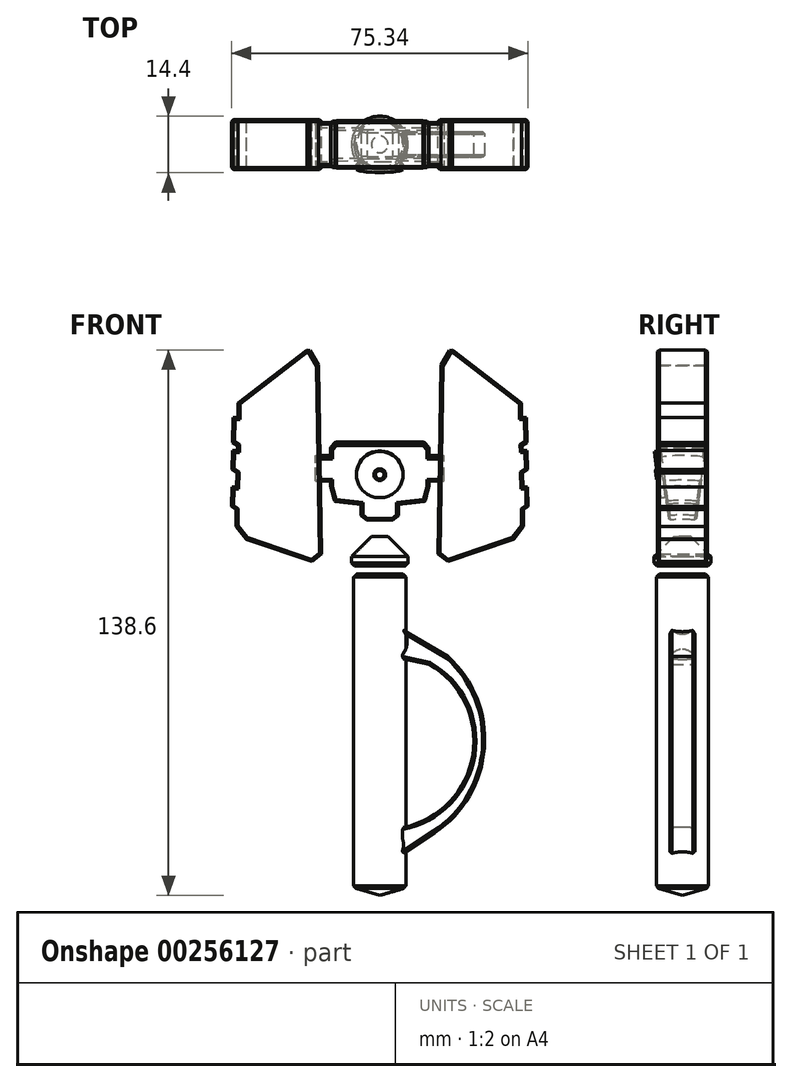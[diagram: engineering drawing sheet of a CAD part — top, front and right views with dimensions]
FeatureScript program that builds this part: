
annotation { "Feature Type Name" : "Feature", "Feature Type Description" : "" }
export const myFeature = defineFeature(function(context is Context, id is Id, definition is map)
    precondition{}
    {
        {
            var Q0;
            Q0=qCreatedBy(makeId("Front.planeOp"),FACE);
            var sketch = newSketch(context, id + "F0", { "sketchPlane" : qUnion([Q0])});
            skLineSegment(sketch, "E0", {"start": v(0, 0) * mm, "end": v(0, 58.8) * mm});
            skLineSegment(sketch, "E1", {"start": v(-12.47, 45.18) * mm, "end": v(-12.47, 35.46) * mm});
            skLineSegment(sketch, "E2", {"start": v(-12.47, 35.46) * mm, "end": v(-11.52, 31.82) * mm});
            skLineSegment(sketch, "E3", {"start": v(-11.52, 31.82) * mm, "end": v(-4.75, 31.04) * mm});
            skLineSegment(sketch, "E4", {"start": v(-4.75, 31.04) * mm, "end": v(-4.75, 28.09) * mm});
            skLineSegment(sketch, "E5", {"start": v(-4.75, 28.09) * mm, "end": v(-3.27, 26.96) * mm});
            skLineSegment(sketch, "E6", {"start": v(-3.27, 26.96) * mm, "end": v(0, 26.96) * mm});
            skLineSegment(sketch, "E7", {"start": v(-12.47, 45.18) * mm, "end": v(-11.17, 46.66) * mm});
            skLineSegment(sketch, "E8", {"start": v(-11.17, 46.66) * mm, "end": v(0, 46.66) * mm});
            skLineSegment(sketch, "E9.MirrorCS", {"start": v(4.75, 28.09) * mm, "end": v(3.27, 26.96) * mm});
            skLineSegment(sketch, "E10.MirrorCS", {"start": v(12.47, 45.18) * mm, "end": v(11.17, 46.66) * mm});
            skLineSegment(sketch, "E11.MirrorCS", {"start": v(11.52, 31.82) * mm, "end": v(4.75, 31.04) * mm});
            skLineSegment(sketch, "E12.MirrorCS", {"start": v(11.17, 46.66) * mm, "end": v(0, 46.66) * mm});
            skLineSegment(sketch, "E13.MirrorCS", {"start": v(12.47, 35.46) * mm, "end": v(11.52, 31.82) * mm});
            skLineSegment(sketch, "E14.MirrorCS", {"start": v(4.75, 31.04) * mm, "end": v(4.75, 28.09) * mm});
            skLineSegment(sketch, "E15.MirrorCS", {"start": v(12.47, 45.18) * mm, "end": v(12.47, 35.46) * mm});
            skLineSegment(sketch, "E16.MirrorCS", {"start": v(3.27, 26.96) * mm, "end": v(0, 26.96) * mm});
            skLineSegment(sketch, "E17", {"start": v(-12.47, 36.94) * mm, "end": v(-16.32, 36.94) * mm});
            skLineSegment(sketch, "E18", {"start": v(-16.32, 36.94) * mm, "end": v(-16.32, 43.2) * mm});
            skLineSegment(sketch, "E19", {"start": v(-16.32, 43.2) * mm, "end": v(-12.47, 43.2) * mm});
            skLineSegment(sketch, "E20.MirrorCS", {"start": v(16.32, 43.2) * mm, "end": v(12.47, 43.2) * mm});
            skLineSegment(sketch, "E21.MirrorCS", {"start": v(16.32, 36.94) * mm, "end": v(16.32, 43.2) * mm});
            skLineSegment(sketch, "E22.MirrorCS", {"start": v(12.47, 36.94) * mm, "end": v(16.32, 36.94) * mm});
            skLineSegment(sketch, "E23", {"start": v(0, 0) * mm, "end": v(-10.1, 0) * mm});
            skLineSegment(sketch, "E24", {"start": v(-12.47, 40.32) * mm, "end": v(-11.54, 40.32) * mm});
            skPoint(sketch, "E24.endSnap0", {"position": v(-12.47, 40.32) * mm});
            skCircle(sketch, "E25", {"center": v(0, 40.32) * mm, "radius": 4.75 * mm});
            skSolve(sketch);
        }
        {
            var Q0;
            Q0=makeQuery(id+"F0.imprint","IMPRINT",FACE,{"disambiguationData":[TD([[makeQuery(id+"F0.imprint","IMPRINT",EDGE,{"derivedFrom":sQuery(id+"F0.wireOp",EDGE,"E9.MirrorCS")}),-1.0]])]});
            var Q1;
            {var subQ0=sQuery(id+"F0.wireOp",EDGE,"E20.MirrorCS");Q1=makeQuery(id+"F0.imprint","IMPRINT",FACE,{"disambiguationData":[TD([[makeQuery(id+"F0.imprint","IMPRINT",EDGE,{"derivedFrom":subQ0}),1.0]])]});}
            var Q2;
            {var subQ1=sQuery(id+"F0.wireOp",EDGE,"E2");Q2=makeQuery(id+"F0.imprint","IMPRINT",FACE,{"disambiguationData":[TD([[makeQuery(id+"F0.imprint","IMPRINT",EDGE,{"derivedFrom":subQ1}),1.0]])]});}
            var Q3;
            {var subQ0=sQuery(id+"F0.wireOp",EDGE,"E25");var subQ1=sQuery(id+"F0.wireOp",EDGE,"E0");var subQ2=makeQuery(id+"F0.imprint","INTERSECT",VERTEX,{"disambiguationData":[OD(0.0)],"derivedFrom":[subQ1,subQ0]});Q3=makeQuery(id+"F0.imprint","IMPRINT",FACE,{"disambiguationData":[TD([[makeQuery(id+"F0.imprint","IMPRINT",EDGE,{"disambiguationData":[TD([[subQ2,-1.0]])],"derivedFrom":subQ1}),-1.0]])]});}
            var Q4;
            {var subQ0=sQuery(id+"F0.wireOp",EDGE,"E17");Q4=makeQuery(id+"F0.imprint","IMPRINT",FACE,{"disambiguationData":[TD([[makeQuery(id+"F0.imprint","IMPRINT",EDGE,{"derivedFrom":subQ0}),-1.0]])]});}
            var Q5;
            {var subQ0=sQuery(id+"F0.wireOp",EDGE,"E25");var subQ1=sQuery(id+"F0.wireOp",EDGE,"E0");var subQ2=makeQuery(id+"F0.imprint","INTERSECT",VERTEX,{"disambiguationData":[OD(0.0)],"derivedFrom":[subQ1,subQ0]});Q5=makeQuery(id+"F0.imprint","IMPRINT",FACE,{"disambiguationData":[TD([[makeQuery(id+"F0.imprint","IMPRINT",EDGE,{"disambiguationData":[TD([[subQ2,-1.0]])],"derivedFrom":subQ1}),1.0]])]});}
            var Q6;
            Q6 = qSketchRegion(id + "F10", true);
            var Q7;
            Q7=sQuery(id+"F0.wireOp",EDGE,"E23");
            revolve(context, id + "F1", {"entities" : qUnion([Q0, Q1, Q2, Q3, Q4, Q5, Q6]), "axis" : qUnion([Q7]), "revolveType" : RevolveType.SYMMETRIC, "angle" : 15 * degree});
        }
        {
            var Q0;
            Q0=qCreatedBy(makeId("Front.planeOp"),FACE);
            var sketch = newSketch(context, id + "F2", { "sketchPlane" : qUnion([Q0])});
            skLineSegment(sketch, "E26", {"start": v(0, 0) * mm, "end": v(0, 63.23) * mm});
            skLineSegment(sketch, "E27", {"start": v(0, 0) * mm, "end": v(-17.13, 0) * mm});
            skLineSegment(sketch, "E28", {"start": v(-14.74, 18.15) * mm, "end": v(-15.53, 66.1) * mm});
            skLineSegment(sketch, "E29", {"start": v(-15.53, 66.1) * mm, "end": v(-18.04, 70.4) * mm});
            skLineSegment(sketch, "E30", {"start": v(-18.04, 70.4) * mm, "end": v(-35.96, 56.53) * mm});
            skLineSegment(sketch, "E31", {"start": v(-35.96, 56.53) * mm, "end": v(-36.55, 25.2) * mm});
            skLineSegment(sketch, "E32", {"start": v(-36.55, 25.2) * mm, "end": v(-33.94, 21.9) * mm});
            skLineSegment(sketch, "E33", {"start": v(-33.94, 21.9) * mm, "end": v(-17.27, 16.26) * mm});
            skLineSegment(sketch, "E34", {"start": v(-17.27, 16.26) * mm, "end": v(-14.74, 18.15) * mm});
            skLineSegment(sketch, "E35", {"start": v(-36.47, 29.48) * mm, "end": v(-37.67, 30.3) * mm});
            skLineSegment(sketch, "E36", {"start": v(-37.67, 30.3) * mm, "end": v(-37.58, 35.2) * mm});
            skLineSegment(sketch, "E37", {"start": v(-37.58, 35.2) * mm, "end": v(-36.36, 35.2) * mm});
            skLineSegment(sketch, "E38", {"start": v(-36.3, 38.8) * mm, "end": v(-37.52, 39.62) * mm});
            skLineSegment(sketch, "E39", {"start": v(-37.52, 39.62) * mm, "end": v(-37.43, 44.52) * mm});
            skLineSegment(sketch, "E40", {"start": v(-37.43, 44.52) * mm, "end": v(-36.19, 44.52) * mm});
            skLineSegment(sketch, "E41", {"start": v(-36.16, 45.72) * mm, "end": v(-37.41, 46.56) * mm});
            skLineSegment(sketch, "E42", {"start": v(-37.41, 46.56) * mm, "end": v(-37.3, 52.8) * mm});
            skLineSegment(sketch, "E43", {"start": v(-37.3, 52.8) * mm, "end": v(-36.03, 52.8) * mm});
            skLineSegment(sketch, "E44.MirrorCS", {"start": v(37.58, 35.2) * mm, "end": v(36.36, 35.2) * mm});
            skLineSegment(sketch, "E45.MirrorCS", {"start": v(36.16, 45.72) * mm, "end": v(37.41, 46.56) * mm});
            skLineSegment(sketch, "E46.MirrorCS", {"start": v(37.43, 44.52) * mm, "end": v(36.19, 44.52) * mm});
            skLineSegment(sketch, "E47.MirrorCS", {"start": v(37.3, 52.8) * mm, "end": v(36.03, 52.8) * mm});
            skLineSegment(sketch, "E48.MirrorCS", {"start": v(36.3, 38.8) * mm, "end": v(37.52, 39.62) * mm});
            skLineSegment(sketch, "E49.MirrorCS", {"start": v(36.47, 29.48) * mm, "end": v(37.67, 30.3) * mm});
            skLineSegment(sketch, "E50.MirrorCS", {"start": v(37.52, 39.62) * mm, "end": v(37.43, 44.52) * mm});
            skLineSegment(sketch, "E51.MirrorCS", {"start": v(37.41, 46.56) * mm, "end": v(37.3, 52.8) * mm});
            skLineSegment(sketch, "E52.MirrorCS", {"start": v(37.67, 30.3) * mm, "end": v(37.58, 35.2) * mm});
            skLineSegment(sketch, "E53.MirrorCS", {"start": v(36.55, 25.2) * mm, "end": v(33.94, 21.9) * mm});
            skLineSegment(sketch, "E54.MirrorCS", {"start": v(33.94, 21.9) * mm, "end": v(17.27, 16.26) * mm});
            skLineSegment(sketch, "E55.MirrorCS", {"start": v(14.74, 18.15) * mm, "end": v(15.53, 66.1) * mm});
            skLineSegment(sketch, "E56.MirrorCS", {"start": v(17.27, 16.26) * mm, "end": v(14.74, 18.15) * mm});
            skLineSegment(sketch, "E57.MirrorCS", {"start": v(35.96, 56.53) * mm, "end": v(36.55, 25.2) * mm});
            skLineSegment(sketch, "E58.MirrorCS", {"start": v(15.53, 66.1) * mm, "end": v(18.04, 70.4) * mm});
            skLineSegment(sketch, "E59.MirrorCS", {"start": v(18.04, 70.4) * mm, "end": v(35.96, 56.53) * mm});
            skSolve(sketch);
        }
        {
            var Q0;
            Q0 = qSketchRegion(id + "F2", true);
            extrude(context, id + "F3", {"entities" : qUnion([Q0]), "endBound" : BoundingType.SYMMETRIC, "depth" : 12.7 * mm});
        }
        {
            var Q0;
            Q0=makeQuery(id+"F3.opExtrude","CAP_EDGE",EDGE,{"disambiguationData":[OSD([sQuery(id+"F2.wireOp",EDGE,"E30")])],"isStart":false});
            var Q1;
            Q1=makeQuery(id+"F3.opExtrude","CAP_EDGE",EDGE,{"disambiguationData":[OSD([sQuery(id+"F2.wireOp",EDGE,"E29")])],"isStart":false});
            var Q2;
            Q2=makeQuery(id+"F3.opExtrude","CAP_EDGE",EDGE,{"disambiguationData":[OSD([sQuery(id+"F2.wireOp",EDGE,"E28")])],"isStart":false});
            var Q3;
            Q3=makeQuery(id+"F3.opExtrude","CAP_EDGE",EDGE,{"disambiguationData":[OSD([sQuery(id+"F2.wireOp",EDGE,"E34")])],"isStart":false});
            var Q4;
            Q4=makeQuery(id+"F3.opExtrude","CAP_EDGE",EDGE,{"disambiguationData":[OSD([sQuery(id+"F2.wireOp",EDGE,"E33")])],"isStart":false});
            var Q5;
            Q5=makeQuery(id+"F3.opExtrude","CAP_EDGE",EDGE,{"disambiguationData":[OSD([sQuery(id+"F2.wireOp",EDGE,"E32")])],"isStart":false});
            var Q6;
            {var subQ0=sQuery(id+"F2.wireOp",EDGE,"E31");Q6=makeQuery(id+"F3.opExtrude","CAP_EDGE",EDGE,{"disambiguationData":[OSD([subQ0]),TDD([makeQuery(id+"F2.imprint","IMPRINT",EDGE,{"disambiguationData":[TD([[makeQuery(id+"F2.imprint","INTERSECT",VERTEX,{"derivedFrom":[subQ0,sQuery(id+"F2.wireOp",EDGE,"E32")]}),1.0]])],"derivedFrom":subQ0})])],"isStart":false});}
            var Q7;
            Q7=makeQuery(id+"F3.opExtrude","CAP_EDGE",EDGE,{"disambiguationData":[OSD([sQuery(id+"F2.wireOp",EDGE,"E35")])],"isStart":false});
            var Q8;
            Q8=makeQuery(id+"F3.opExtrude","CAP_EDGE",EDGE,{"disambiguationData":[OSD([sQuery(id+"F2.wireOp",EDGE,"E36")])],"isStart":false});
            var Q9;
            Q9=makeQuery(id+"F3.opExtrude","CAP_EDGE",EDGE,{"disambiguationData":[OSD([sQuery(id+"F2.wireOp",EDGE,"E37")])],"isStart":false});
            var Q10;
            {var subQ0=sQuery(id+"F2.wireOp",EDGE,"E31");Q10=makeQuery(id+"F3.opExtrude","CAP_EDGE",EDGE,{"disambiguationData":[OSD([subQ0]),TDD([makeQuery(id+"F2.imprint","IMPRINT",EDGE,{"disambiguationData":[TD([[makeQuery(id+"F2.imprint","INTERSECT",VERTEX,{"derivedFrom":[subQ0,sQuery(id+"F2.wireOp",EDGE,"E37")]}),1.0]])],"derivedFrom":subQ0})])],"isStart":false});}
            var Q11;
            Q11=makeQuery(id+"F3.opExtrude","CAP_EDGE",EDGE,{"disambiguationData":[OSD([sQuery(id+"F2.wireOp",EDGE,"E38")])],"isStart":false});
            var Q12;
            Q12=makeQuery(id+"F3.opExtrude","CAP_EDGE",EDGE,{"disambiguationData":[OSD([sQuery(id+"F2.wireOp",EDGE,"E39")])],"isStart":false});
            var Q13;
            Q13=makeQuery(id+"F3.opExtrude","CAP_EDGE",EDGE,{"disambiguationData":[OSD([sQuery(id+"F2.wireOp",EDGE,"E40")])],"isStart":false});
            var Q14;
            {var subQ0=sQuery(id+"F2.wireOp",EDGE,"E31");Q14=makeQuery(id+"F3.opExtrude","CAP_EDGE",EDGE,{"disambiguationData":[OSD([subQ0]),TDD([makeQuery(id+"F2.imprint","IMPRINT",EDGE,{"disambiguationData":[TD([[makeQuery(id+"F2.imprint","INTERSECT",VERTEX,{"derivedFrom":[subQ0,sQuery(id+"F2.wireOp",EDGE,"E40")]}),1.0]])],"derivedFrom":subQ0})])],"isStart":false});}
            var Q15;
            Q15=makeQuery(id+"F3.opExtrude","CAP_EDGE",EDGE,{"disambiguationData":[OSD([sQuery(id+"F2.wireOp",EDGE,"E41")])],"isStart":false});
            var Q16;
            Q16=makeQuery(id+"F3.opExtrude","CAP_EDGE",EDGE,{"disambiguationData":[OSD([sQuery(id+"F2.wireOp",EDGE,"E42")])],"isStart":false});
            var Q17;
            Q17=makeQuery(id+"F3.opExtrude","CAP_EDGE",EDGE,{"disambiguationData":[OSD([sQuery(id+"F2.wireOp",EDGE,"E43")])],"isStart":false});
            var Q18;
            {var subQ0=sQuery(id+"F2.wireOp",EDGE,"E31");Q18=makeQuery(id+"F3.opExtrude","CAP_EDGE",EDGE,{"disambiguationData":[OSD([subQ0]),TDD([makeQuery(id+"F2.imprint","IMPRINT",EDGE,{"disambiguationData":[TD([[makeQuery(id+"F2.imprint","INTERSECT",VERTEX,{"derivedFrom":[sQuery(id+"F2.wireOp",EDGE,"E30"),subQ0]}),-1.0]])],"derivedFrom":subQ0})])],"isStart":false});}
            var Q19;
            Q19=makeQuery(id+"F3.opExtrude","CAP_EDGE",EDGE,{"disambiguationData":[OSD([sQuery(id+"F2.wireOp",EDGE,"E59.MirrorCS")])],"isStart":false});
            var Q20;
            {var subQ0=sQuery(id+"F2.wireOp",EDGE,"E57.MirrorCS");Q20=makeQuery(id+"F3.opExtrude","CAP_EDGE",EDGE,{"disambiguationData":[OSD([subQ0]),TDD([makeQuery(id+"F2.imprint","IMPRINT",EDGE,{"disambiguationData":[TD([[makeQuery(id+"F2.imprint","INTERSECT",VERTEX,{"derivedFrom":[sQuery(id+"F2.wireOp",EDGE,"E47.MirrorCS"),subQ0]}),1.0]])],"derivedFrom":subQ0})])],"isStart":false});}
            var Q21;
            Q21=makeQuery(id+"F3.opExtrude","CAP_EDGE",EDGE,{"disambiguationData":[OSD([sQuery(id+"F2.wireOp",EDGE,"E47.MirrorCS")])],"isStart":false});
            var Q22;
            Q22=makeQuery(id+"F3.opExtrude","CAP_EDGE",EDGE,{"disambiguationData":[OSD([sQuery(id+"F2.wireOp",EDGE,"E51.MirrorCS")])],"isStart":false});
            var Q23;
            Q23=makeQuery(id+"F3.opExtrude","CAP_EDGE",EDGE,{"disambiguationData":[OSD([sQuery(id+"F2.wireOp",EDGE,"E45.MirrorCS")])],"isStart":false});
            var Q24;
            {var subQ0=sQuery(id+"F2.wireOp",EDGE,"E57.MirrorCS");Q24=makeQuery(id+"F3.opExtrude","CAP_EDGE",EDGE,{"disambiguationData":[OSD([subQ0]),TDD([makeQuery(id+"F2.imprint","IMPRINT",EDGE,{"disambiguationData":[TD([[makeQuery(id+"F2.imprint","INTERSECT",VERTEX,{"derivedFrom":[sQuery(id+"F2.wireOp",EDGE,"E46.MirrorCS"),subQ0]}),1.0]])],"derivedFrom":subQ0})])],"isStart":false});}
            var Q25;
            Q25=makeQuery(id+"F3.opExtrude","CAP_EDGE",EDGE,{"disambiguationData":[OSD([sQuery(id+"F2.wireOp",EDGE,"E46.MirrorCS")])],"isStart":false});
            var Q26;
            Q26=makeQuery(id+"F3.opExtrude","CAP_EDGE",EDGE,{"disambiguationData":[OSD([sQuery(id+"F2.wireOp",EDGE,"E50.MirrorCS")])],"isStart":false});
            var Q27;
            Q27=makeQuery(id+"F3.opExtrude","CAP_EDGE",EDGE,{"disambiguationData":[OSD([sQuery(id+"F2.wireOp",EDGE,"E48.MirrorCS")])],"isStart":false});
            var Q28;
            {var subQ0=sQuery(id+"F2.wireOp",EDGE,"E57.MirrorCS");Q28=makeQuery(id+"F3.opExtrude","CAP_EDGE",EDGE,{"disambiguationData":[OSD([subQ0]),TDD([makeQuery(id+"F2.imprint","IMPRINT",EDGE,{"disambiguationData":[TD([[makeQuery(id+"F2.imprint","INTERSECT",VERTEX,{"derivedFrom":[sQuery(id+"F2.wireOp",EDGE,"E44.MirrorCS"),subQ0]}),1.0]])],"derivedFrom":subQ0})])],"isStart":false});}
            var Q29;
            Q29=makeQuery(id+"F3.opExtrude","CAP_EDGE",EDGE,{"disambiguationData":[OSD([sQuery(id+"F2.wireOp",EDGE,"E44.MirrorCS")])],"isStart":false});
            var Q30;
            Q30=makeQuery(id+"F3.opExtrude","CAP_EDGE",EDGE,{"disambiguationData":[OSD([sQuery(id+"F2.wireOp",EDGE,"E52.MirrorCS")])],"isStart":false});
            var Q31;
            {var subQ0=sQuery(id+"F2.wireOp",EDGE,"E57.MirrorCS");Q31=makeQuery(id+"F3.opExtrude","CAP_EDGE",EDGE,{"disambiguationData":[OSD([subQ0]),TDD([makeQuery(id+"F2.imprint","IMPRINT",EDGE,{"disambiguationData":[TD([[makeQuery(id+"F2.imprint","INTERSECT",VERTEX,{"derivedFrom":[sQuery(id+"F2.wireOp",EDGE,"E49.MirrorCS"),subQ0]}),-1.0]])],"derivedFrom":subQ0})])],"isStart":false});}
            var Q32;
            Q32=makeQuery(id+"F3.opExtrude","CAP_EDGE",EDGE,{"disambiguationData":[OSD([sQuery(id+"F2.wireOp",EDGE,"E49.MirrorCS")])],"isStart":false});
            var Q33;
            Q33=makeQuery(id+"F3.opExtrude","CAP_EDGE",EDGE,{"disambiguationData":[OSD([sQuery(id+"F2.wireOp",EDGE,"E53.MirrorCS")])],"isStart":false});
            var Q34;
            Q34=makeQuery(id+"F3.opExtrude","CAP_EDGE",EDGE,{"disambiguationData":[OSD([sQuery(id+"F2.wireOp",EDGE,"E54.MirrorCS")])],"isStart":false});
            var Q35;
            Q35=makeQuery(id+"F3.opExtrude","CAP_EDGE",EDGE,{"disambiguationData":[OSD([sQuery(id+"F2.wireOp",EDGE,"E56.MirrorCS")])],"isStart":false});
            var Q36;
            Q36=makeQuery(id+"F3.opExtrude","CAP_EDGE",EDGE,{"disambiguationData":[OSD([sQuery(id+"F2.wireOp",EDGE,"E55.MirrorCS")])],"isStart":false});
            var Q37;
            Q37=makeQuery(id+"F3.opExtrude","CAP_EDGE",EDGE,{"disambiguationData":[OSD([sQuery(id+"F2.wireOp",EDGE,"E58.MirrorCS")])],"isStart":false});
            var Q38;
            Q38=makeQuery(id+"F3.opExtrude","CAP_EDGE",EDGE,{"disambiguationData":[OSD([sQuery(id+"F2.wireOp",EDGE,"E59.MirrorCS")])],"isStart":true});
            var Q39;
            Q39=makeQuery(id+"F3.opExtrude","CAP_FACE",FACE,{"disambiguationData":[OSD([sQuery(id+"F2.wireOp",EDGE,"E47.MirrorCS"),sQuery(id+"F2.wireOp",EDGE,"E44.MirrorCS"),sQuery(id+"F2.wireOp",EDGE,"E46.MirrorCS"),sQuery(id+"F2.wireOp",EDGE,"E48.MirrorCS"),sQuery(id+"F2.wireOp",EDGE,"E49.MirrorCS"),sQuery(id+"F2.wireOp",EDGE,"E45.MirrorCS"),sQuery(id+"F2.wireOp",EDGE,"E53.MirrorCS"),sQuery(id+"F2.wireOp",EDGE,"E54.MirrorCS"),sQuery(id+"F2.wireOp",EDGE,"E55.MirrorCS"),sQuery(id+"F2.wireOp",EDGE,"E52.MirrorCS"),sQuery(id+"F2.wireOp",EDGE,"E56.MirrorCS"),sQuery(id+"F2.wireOp",EDGE,"E57.MirrorCS"),sQuery(id+"F2.wireOp",EDGE,"E58.MirrorCS"),sQuery(id+"F2.wireOp",EDGE,"E50.MirrorCS"),sQuery(id+"F2.wireOp",EDGE,"E59.MirrorCS"),sQuery(id+"F2.wireOp",EDGE,"E51.MirrorCS")])],"isStart":true});
            var Q40;
            Q40=makeQuery(id+"F3.opExtrude","CAP_FACE",FACE,{"disambiguationData":[OSD([sQuery(id+"F2.wireOp",EDGE,"E28"),sQuery(id+"F2.wireOp",EDGE,"E29"),sQuery(id+"F2.wireOp",EDGE,"E30"),sQuery(id+"F2.wireOp",EDGE,"E31"),sQuery(id+"F2.wireOp",EDGE,"E32"),sQuery(id+"F2.wireOp",EDGE,"E33"),sQuery(id+"F2.wireOp",EDGE,"E34"),sQuery(id+"F2.wireOp",EDGE,"E35"),sQuery(id+"F2.wireOp",EDGE,"E36"),sQuery(id+"F2.wireOp",EDGE,"E37"),sQuery(id+"F2.wireOp",EDGE,"E38"),sQuery(id+"F2.wireOp",EDGE,"E39"),sQuery(id+"F2.wireOp",EDGE,"E40"),sQuery(id+"F2.wireOp",EDGE,"E41"),sQuery(id+"F2.wireOp",EDGE,"E42"),sQuery(id+"F2.wireOp",EDGE,"E43")])],"isStart":true});
            var Q41;
            Q41=makeQuery(id+"F3.opExtrude","SWEPT_EDGE",EDGE,{"disambiguationData":[OSD([sQuery(id+"F2.wireOp",EDGE,"E29"),sQuery(id+"F2.wireOp",EDGE,"E30")])]});
            var Q42;
            Q42=makeQuery(id+"F3.opExtrude","SWEPT_EDGE",EDGE,{"disambiguationData":[OSD([sQuery(id+"F2.wireOp",EDGE,"E28"),sQuery(id+"F2.wireOp",EDGE,"E29")])]});
            var Q43;
            Q43=makeQuery(id+"F3.opExtrude","SWEPT_EDGE",EDGE,{"disambiguationData":[OSD([sQuery(id+"F2.wireOp",EDGE,"E58.MirrorCS"),sQuery(id+"F2.wireOp",EDGE,"E59.MirrorCS")])]});
            var Q44;
            Q44=makeQuery(id+"F3.opExtrude","SWEPT_EDGE",EDGE,{"disambiguationData":[OSD([sQuery(id+"F2.wireOp",EDGE,"E55.MirrorCS"),sQuery(id+"F2.wireOp",EDGE,"E58.MirrorCS")])]});
            var Q45;
            Q45=makeQuery(id+"F3.opExtrude","SWEPT_EDGE",EDGE,{"disambiguationData":[OSD([sQuery(id+"F2.wireOp",EDGE,"E32"),sQuery(id+"F2.wireOp",EDGE,"E33")])]});
            var Q46;
            Q46=makeQuery(id+"F3.opExtrude","SWEPT_EDGE",EDGE,{"disambiguationData":[OSD([sQuery(id+"F2.wireOp",EDGE,"E53.MirrorCS"),sQuery(id+"F2.wireOp",EDGE,"E54.MirrorCS")])]});
            chamfer(context, id + "F4", {"entities" : qUnion([Q0, Q1, Q2, Q3, Q4, Q5, Q6, Q7, Q8, Q9, Q10, Q11, Q12, Q13, Q14, Q15, Q16, Q17, Q18, Q19, Q20, Q21, Q22, Q23, Q24, Q25, Q26, Q27, Q28, Q29, Q30, Q31, Q32, Q33, Q34, Q35, Q36, Q37, Q38, Q39, Q40, Q41, Q42, Q43, Q44, Q45, Q46]), "width" : 0.5 * mm, "tangentPropagation" : true});
        }
        {
            var Q0;
            Q0=makeQuery(id+"F1.opRevolve","CAP_FACE",FACE,{"disambiguationData":[OSD([sQuery(id+"F0.wireOp",EDGE,"E1"),sQuery(id+"F0.wireOp",EDGE,"E2"),sQuery(id+"F0.wireOp",EDGE,"E3"),sQuery(id+"F0.wireOp",EDGE,"E4"),sQuery(id+"F0.wireOp",EDGE,"E5"),sQuery(id+"F0.wireOp",EDGE,"E6"),sQuery(id+"F0.wireOp",EDGE,"E7"),sQuery(id+"F0.wireOp",EDGE,"E8"),sQuery(id+"F0.wireOp",EDGE,"E9.MirrorCS"),sQuery(id+"F0.wireOp",EDGE,"E10.MirrorCS"),sQuery(id+"F0.wireOp",EDGE,"E11.MirrorCS"),sQuery(id+"F0.wireOp",EDGE,"E12.MirrorCS"),sQuery(id+"F0.wireOp",EDGE,"E13.MirrorCS"),sQuery(id+"F0.wireOp",EDGE,"E14.MirrorCS"),sQuery(id+"F0.wireOp",EDGE,"E15.MirrorCS"),sQuery(id+"F0.wireOp",EDGE,"E16.MirrorCS"),sQuery(id+"F0.wireOp",EDGE,"E17"),sQuery(id+"F0.wireOp",EDGE,"E18"),sQuery(id+"F0.wireOp",EDGE,"E19"),sQuery(id+"F0.wireOp",EDGE,"E20.MirrorCS"),sQuery(id+"F0.wireOp",EDGE,"E21.MirrorCS"),sQuery(id+"F0.wireOp",EDGE,"E22.MirrorCS")])],"isStart":true});
            var sketch = newSketch(context, id + "F5", { "sketchPlane" : qUnion([Q0])});
            skCircle(sketch, "E60", {"center": v(0, 38.85) * mm, "radius": 5.92 * mm});
            skCircle(sketch, "E61", {"center": v(0, 38.85) * mm, "radius": 1.63 * mm});
            skSolve(sketch);
        }
        {
            var Q0;
            Q0=makeQuery(id+"F5.imprint","IMPRINT",FACE,{"disambiguationData":[TD([[makeQuery(id+"F5.imprint","IMPRINT",EDGE,{"derivedFrom":sQuery(id+"F5.wireOp",EDGE,"E60")}),1.0]])]});
            extrude(context, id + "F6", {"entities" : qUnion([Q0]), "operationType" : NewBodyOperationType.ADD, "depth" : 1.27 * mm});
        }
        {
            var Q0;
            Q0=makeQuery(id+"F6.boolean.opBoolean","SPLIT",FACE,{"disambiguationData":[TD([makeQuery(id+"F6.opExtrude","SWEPT_FACE",FACE,{"disambiguationData":[OSD([sQuery(id+"F5.wireOp",EDGE,"E61")])]})])],"derivedFrom":makeQuery(id+"F1.opRevolve","CAP_FACE",FACE,{"disambiguationData":[OSD([sQuery(id+"F0.wireOp",EDGE,"E1"),sQuery(id+"F0.wireOp",EDGE,"E2"),sQuery(id+"F0.wireOp",EDGE,"E3"),sQuery(id+"F0.wireOp",EDGE,"E4"),sQuery(id+"F0.wireOp",EDGE,"E5"),sQuery(id+"F0.wireOp",EDGE,"E6"),sQuery(id+"F0.wireOp",EDGE,"E7"),sQuery(id+"F0.wireOp",EDGE,"E8"),sQuery(id+"F0.wireOp",EDGE,"E9.MirrorCS"),sQuery(id+"F0.wireOp",EDGE,"E10.MirrorCS"),sQuery(id+"F0.wireOp",EDGE,"E11.MirrorCS"),sQuery(id+"F0.wireOp",EDGE,"E12.MirrorCS"),sQuery(id+"F0.wireOp",EDGE,"E13.MirrorCS"),sQuery(id+"F0.wireOp",EDGE,"E14.MirrorCS"),sQuery(id+"F0.wireOp",EDGE,"E15.MirrorCS"),sQuery(id+"F0.wireOp",EDGE,"E16.MirrorCS"),sQuery(id+"F0.wireOp",EDGE,"E17"),sQuery(id+"F0.wireOp",EDGE,"E18"),sQuery(id+"F0.wireOp",EDGE,"E19"),sQuery(id+"F0.wireOp",EDGE,"E20.MirrorCS"),sQuery(id+"F0.wireOp",EDGE,"E21.MirrorCS"),sQuery(id+"F0.wireOp",EDGE,"E22.MirrorCS")])],"isStart":true})});
            extrude(context, id + "F7", {"entities" : qUnion([Q0]), "operationType" : NewBodyOperationType.ADD, "depth" : 1.65 * mm});
        }
        {
            var Q0;
            Q0=makeQuery(id+"F7.opExtrude","CAP_FACE",FACE,{"disambiguationData":[OSD([sQuery(id+"F0.wireOp",EDGE,"E1"),sQuery(id+"F0.wireOp",EDGE,"E2"),sQuery(id+"F0.wireOp",EDGE,"E3"),sQuery(id+"F0.wireOp",EDGE,"E4"),sQuery(id+"F0.wireOp",EDGE,"E5"),sQuery(id+"F0.wireOp",EDGE,"E6"),sQuery(id+"F0.wireOp",EDGE,"E7"),sQuery(id+"F0.wireOp",EDGE,"E8"),sQuery(id+"F0.wireOp",EDGE,"E9.MirrorCS"),sQuery(id+"F0.wireOp",EDGE,"E10.MirrorCS"),sQuery(id+"F0.wireOp",EDGE,"E11.MirrorCS"),sQuery(id+"F0.wireOp",EDGE,"E12.MirrorCS"),sQuery(id+"F0.wireOp",EDGE,"E13.MirrorCS"),sQuery(id+"F0.wireOp",EDGE,"E14.MirrorCS"),sQuery(id+"F0.wireOp",EDGE,"E15.MirrorCS"),sQuery(id+"F0.wireOp",EDGE,"E16.MirrorCS"),sQuery(id+"F0.wireOp",EDGE,"E17"),sQuery(id+"F0.wireOp",EDGE,"E18"),sQuery(id+"F0.wireOp",EDGE,"E19"),sQuery(id+"F0.wireOp",EDGE,"E20.MirrorCS"),sQuery(id+"F0.wireOp",EDGE,"E21.MirrorCS"),sQuery(id+"F0.wireOp",EDGE,"E22.MirrorCS")])],"isStart":false});
            chamfer(context, id + "F8", {"entities" : qUnion([Q0]), "width" : 0.5 * mm, "tangentPropagation" : true});
        }
        {
            var Q0;
            Q0=makeQuery(id+"F1.opRevolve","CAP_EDGE",EDGE,{"disambiguationData":[OSD([sQuery(id+"F0.wireOp",EDGE,"E8"),sQuery(id+"F0.wireOp",EDGE,"E12.MirrorCS")])],"isStart":true});
            var Q1;
            Q1=makeQuery(id+"F1.opRevolve","CAP_EDGE",EDGE,{"disambiguationData":[OSD([sQuery(id+"F0.wireOp",EDGE,"E10.MirrorCS")])],"isStart":true});
            var Q2;
            {var subQ0=sQuery(id+"F0.wireOp",EDGE,"E15.MirrorCS");Q2=makeQuery(id+"F1.opRevolve","CAP_EDGE",EDGE,{"disambiguationData":[OSD([subQ0]),TDD([makeQuery(id+"F0.imprint","IMPRINT",EDGE,{"disambiguationData":[TD([[makeQuery(id+"F0.imprint","INTERSECT",VERTEX,{"derivedFrom":[sQuery(id+"F0.wireOp",EDGE,"E10.MirrorCS"),subQ0]}),-1.0]])],"derivedFrom":subQ0})])],"isStart":true});}
            var Q3;
            Q3=makeQuery(id+"F1.opRevolve","CAP_EDGE",EDGE,{"disambiguationData":[OSD([sQuery(id+"F0.wireOp",EDGE,"E20.MirrorCS")])],"isStart":true});
            var Q4;
            Q4=makeQuery(id+"F1.opRevolve","CAP_EDGE",EDGE,{"disambiguationData":[OSD([sQuery(id+"F0.wireOp",EDGE,"E22.MirrorCS")])],"isStart":true});
            var Q5;
            {var subQ0=sQuery(id+"F0.wireOp",EDGE,"E15.MirrorCS");Q5=makeQuery(id+"F1.opRevolve","CAP_EDGE",EDGE,{"disambiguationData":[OSD([subQ0]),TDD([makeQuery(id+"F0.imprint","IMPRINT",EDGE,{"disambiguationData":[TD([[makeQuery(id+"F0.imprint","INTERSECT",VERTEX,{"derivedFrom":[sQuery(id+"F0.wireOp",EDGE,"E13.MirrorCS"),subQ0]}),1.0]])],"derivedFrom":subQ0})])],"isStart":true});}
            var Q6;
            Q6=makeQuery(id+"F1.opRevolve","CAP_EDGE",EDGE,{"disambiguationData":[OSD([sQuery(id+"F0.wireOp",EDGE,"E13.MirrorCS")])],"isStart":true});
            var Q7;
            Q7=makeQuery(id+"F1.opRevolve","CAP_EDGE",EDGE,{"disambiguationData":[OSD([sQuery(id+"F0.wireOp",EDGE,"E11.MirrorCS")])],"isStart":true});
            var Q8;
            Q8=makeQuery(id+"F1.opRevolve","CAP_EDGE",EDGE,{"disambiguationData":[OSD([sQuery(id+"F0.wireOp",EDGE,"E14.MirrorCS")])],"isStart":true});
            var Q9;
            Q9=makeQuery(id+"F1.opRevolve","CAP_EDGE",EDGE,{"disambiguationData":[OSD([sQuery(id+"F0.wireOp",EDGE,"E9.MirrorCS")])],"isStart":true});
            var Q10;
            Q10=makeQuery(id+"F1.opRevolve","CAP_EDGE",EDGE,{"disambiguationData":[OSD([sQuery(id+"F0.wireOp",EDGE,"E6"),sQuery(id+"F0.wireOp",EDGE,"E16.MirrorCS")])],"isStart":true});
            var Q11;
            Q11=makeQuery(id+"F1.opRevolve","CAP_EDGE",EDGE,{"disambiguationData":[OSD([sQuery(id+"F0.wireOp",EDGE,"E5")])],"isStart":true});
            var Q12;
            Q12=makeQuery(id+"F1.opRevolve","CAP_EDGE",EDGE,{"disambiguationData":[OSD([sQuery(id+"F0.wireOp",EDGE,"E4")])],"isStart":true});
            var Q13;
            Q13=makeQuery(id+"F1.opRevolve","CAP_EDGE",EDGE,{"disambiguationData":[OSD([sQuery(id+"F0.wireOp",EDGE,"E3")])],"isStart":true});
            var Q14;
            Q14=makeQuery(id+"F1.opRevolve","CAP_EDGE",EDGE,{"disambiguationData":[OSD([sQuery(id+"F0.wireOp",EDGE,"E2")])],"isStart":true});
            var Q15;
            {var subQ0=sQuery(id+"F0.wireOp",EDGE,"E1");Q15=makeQuery(id+"F1.opRevolve","CAP_EDGE",EDGE,{"disambiguationData":[OSD([subQ0]),TDD([makeQuery(id+"F0.imprint","IMPRINT",EDGE,{"disambiguationData":[TD([[makeQuery(id+"F0.imprint","INTERSECT",VERTEX,{"derivedFrom":[subQ0,sQuery(id+"F0.wireOp",EDGE,"E2")]}),1.0]])],"derivedFrom":subQ0})])],"isStart":true});}
            var Q16;
            Q16=makeQuery(id+"F1.opRevolve","CAP_EDGE",EDGE,{"disambiguationData":[OSD([sQuery(id+"F0.wireOp",EDGE,"E17")])],"isStart":true});
            var Q17;
            Q17=makeQuery(id+"F1.opRevolve","CAP_EDGE",EDGE,{"disambiguationData":[OSD([sQuery(id+"F0.wireOp",EDGE,"E18")])],"isStart":true});
            var Q18;
            Q18=makeQuery(id+"F1.opRevolve","CAP_EDGE",EDGE,{"disambiguationData":[OSD([sQuery(id+"F0.wireOp",EDGE,"E19")])],"isStart":true});
            var Q19;
            {var subQ0=sQuery(id+"F0.wireOp",EDGE,"E1");Q19=makeQuery(id+"F1.opRevolve","CAP_EDGE",EDGE,{"disambiguationData":[OSD([subQ0]),TDD([makeQuery(id+"F0.imprint","IMPRINT",EDGE,{"disambiguationData":[TD([[makeQuery(id+"F0.imprint","INTERSECT",VERTEX,{"derivedFrom":[subQ0,sQuery(id+"F0.wireOp",EDGE,"E7")]}),-1.0]])],"derivedFrom":subQ0})])],"isStart":true});}
            var Q20;
            Q20=makeQuery(id+"F1.opRevolve","CAP_EDGE",EDGE,{"disambiguationData":[OSD([sQuery(id+"F0.wireOp",EDGE,"E7")])],"isStart":true});
            var Q21;
            Q21=makeQuery(id+"F1.opRevolve","CAP_EDGE",EDGE,{"disambiguationData":[OSD([sQuery(id+"F0.wireOp",EDGE,"E8"),sQuery(id+"F0.wireOp",EDGE,"E12.MirrorCS")])],"isStart":false});
            var Q22;
            Q22=makeQuery(id+"F1.opRevolve","CAP_EDGE",EDGE,{"disambiguationData":[OSD([sQuery(id+"F0.wireOp",EDGE,"E10.MirrorCS")])],"isStart":false});
            var Q23;
            {var subQ0=sQuery(id+"F0.wireOp",EDGE,"E15.MirrorCS");Q23=makeQuery(id+"F1.opRevolve","CAP_EDGE",EDGE,{"disambiguationData":[OSD([subQ0]),TDD([makeQuery(id+"F0.imprint","IMPRINT",EDGE,{"disambiguationData":[TD([[makeQuery(id+"F0.imprint","INTERSECT",VERTEX,{"derivedFrom":[sQuery(id+"F0.wireOp",EDGE,"E10.MirrorCS"),subQ0]}),-1.0]])],"derivedFrom":subQ0})])],"isStart":false});}
            var Q24;
            Q24=makeQuery(id+"F1.opRevolve","CAP_EDGE",EDGE,{"disambiguationData":[OSD([sQuery(id+"F0.wireOp",EDGE,"E20.MirrorCS")])],"isStart":false});
            var Q25;
            Q25=makeQuery(id+"F1.opRevolve","CAP_EDGE",EDGE,{"disambiguationData":[OSD([sQuery(id+"F0.wireOp",EDGE,"E22.MirrorCS")])],"isStart":false});
            var Q26;
            {var subQ0=sQuery(id+"F0.wireOp",EDGE,"E15.MirrorCS");Q26=makeQuery(id+"F1.opRevolve","CAP_EDGE",EDGE,{"disambiguationData":[OSD([subQ0]),TDD([makeQuery(id+"F0.imprint","IMPRINT",EDGE,{"disambiguationData":[TD([[makeQuery(id+"F0.imprint","INTERSECT",VERTEX,{"derivedFrom":[sQuery(id+"F0.wireOp",EDGE,"E13.MirrorCS"),subQ0]}),1.0]])],"derivedFrom":subQ0})])],"isStart":false});}
            var Q27;
            Q27=makeQuery(id+"F1.opRevolve","CAP_EDGE",EDGE,{"disambiguationData":[OSD([sQuery(id+"F0.wireOp",EDGE,"E13.MirrorCS")])],"isStart":false});
            var Q28;
            Q28=makeQuery(id+"F1.opRevolve","CAP_EDGE",EDGE,{"disambiguationData":[OSD([sQuery(id+"F0.wireOp",EDGE,"E11.MirrorCS")])],"isStart":false});
            var Q29;
            Q29=makeQuery(id+"F1.opRevolve","CAP_EDGE",EDGE,{"disambiguationData":[OSD([sQuery(id+"F0.wireOp",EDGE,"E14.MirrorCS")])],"isStart":false});
            var Q30;
            Q30=makeQuery(id+"F1.opRevolve","CAP_EDGE",EDGE,{"disambiguationData":[OSD([sQuery(id+"F0.wireOp",EDGE,"E9.MirrorCS")])],"isStart":false});
            var Q31;
            Q31=makeQuery(id+"F1.opRevolve","CAP_EDGE",EDGE,{"disambiguationData":[OSD([sQuery(id+"F0.wireOp",EDGE,"E6"),sQuery(id+"F0.wireOp",EDGE,"E16.MirrorCS")])],"isStart":false});
            var Q32;
            Q32=makeQuery(id+"F1.opRevolve","CAP_EDGE",EDGE,{"disambiguationData":[OSD([sQuery(id+"F0.wireOp",EDGE,"E5")])],"isStart":false});
            var Q33;
            Q33=makeQuery(id+"F1.opRevolve","CAP_EDGE",EDGE,{"disambiguationData":[OSD([sQuery(id+"F0.wireOp",EDGE,"E4")])],"isStart":false});
            var Q34;
            Q34=makeQuery(id+"F1.opRevolve","CAP_EDGE",EDGE,{"disambiguationData":[OSD([sQuery(id+"F0.wireOp",EDGE,"E3")])],"isStart":false});
            var Q35;
            Q35=makeQuery(id+"F1.opRevolve","CAP_EDGE",EDGE,{"disambiguationData":[OSD([sQuery(id+"F0.wireOp",EDGE,"E2")])],"isStart":false});
            var Q36;
            {var subQ0=sQuery(id+"F0.wireOp",EDGE,"E1");Q36=makeQuery(id+"F1.opRevolve","CAP_EDGE",EDGE,{"disambiguationData":[OSD([subQ0]),TDD([makeQuery(id+"F0.imprint","IMPRINT",EDGE,{"disambiguationData":[TD([[makeQuery(id+"F0.imprint","INTERSECT",VERTEX,{"derivedFrom":[subQ0,sQuery(id+"F0.wireOp",EDGE,"E2")]}),1.0]])],"derivedFrom":subQ0})])],"isStart":false});}
            var Q37;
            Q37=makeQuery(id+"F1.opRevolve","CAP_EDGE",EDGE,{"disambiguationData":[OSD([sQuery(id+"F0.wireOp",EDGE,"E17")])],"isStart":false});
            var Q38;
            Q38=makeQuery(id+"F1.opRevolve","CAP_EDGE",EDGE,{"disambiguationData":[OSD([sQuery(id+"F0.wireOp",EDGE,"E19")])],"isStart":false});
            var Q39;
            {var subQ0=sQuery(id+"F0.wireOp",EDGE,"E1");Q39=makeQuery(id+"F1.opRevolve","CAP_EDGE",EDGE,{"disambiguationData":[OSD([subQ0]),TDD([makeQuery(id+"F0.imprint","IMPRINT",EDGE,{"disambiguationData":[TD([[makeQuery(id+"F0.imprint","INTERSECT",VERTEX,{"derivedFrom":[subQ0,sQuery(id+"F0.wireOp",EDGE,"E7")]}),-1.0]])],"derivedFrom":subQ0})])],"isStart":false});}
            var Q40;
            Q40=makeQuery(id+"F1.opRevolve","CAP_EDGE",EDGE,{"disambiguationData":[OSD([sQuery(id+"F0.wireOp",EDGE,"E7")])],"isStart":false});
            var Q41;
            Q41=makeQuery(id+"F1.opRevolve","SWEPT_EDGE",EDGE,{"disambiguationData":[OSD([sQuery(id+"F0.wireOp",EDGE,"E10.MirrorCS"),sQuery(id+"F0.wireOp",EDGE,"E12.MirrorCS")])]});
            var Q42;
            Q42=makeQuery(id+"F1.opRevolve","SWEPT_EDGE",EDGE,{"disambiguationData":[OSD([sQuery(id+"F0.wireOp",EDGE,"E10.MirrorCS"),sQuery(id+"F0.wireOp",EDGE,"E15.MirrorCS")])]});
            var Q43;
            Q43=makeQuery(id+"F1.opRevolve","SWEPT_EDGE",EDGE,{"disambiguationData":[OSD([sQuery(id+"F0.wireOp",EDGE,"E1"),sQuery(id+"F0.wireOp",EDGE,"E7")])]});
            var Q44;
            Q44=makeQuery(id+"F1.opRevolve","SWEPT_EDGE",EDGE,{"disambiguationData":[OSD([sQuery(id+"F0.wireOp",EDGE,"E7"),sQuery(id+"F0.wireOp",EDGE,"E8")])]});
            chamfer(context, id + "F9", {"entities" : qUnion([Q0, Q1, Q2, Q3, Q4, Q5, Q6, Q7, Q8, Q9, Q10, Q11, Q12, Q13, Q14, Q15, Q16, Q17, Q18, Q19, Q20, Q21, Q22, Q23, Q24, Q25, Q26, Q27, Q28, Q29, Q30, Q31, Q32, Q33, Q34, Q35, Q36, Q37, Q38, Q39, Q40, Q41, Q42, Q43, Q44]), "width" : 0.5 * mm, "tangentPropagation" : true});
        }
        {
            var Q0;
            Q0=qCreatedBy(makeId("Front.planeOp"),FACE);
            var sketch = newSketch(context, id + "F10", { "sketchPlane" : qUnion([Q0])});
            skLineSegment(sketch, "E62", {"start": v(0, 28.33) * mm, "end": v(0, -68.56) * mm});
            skLineSegment(sketch, "E63", {"start": v(0, -68.56) * mm, "end": v(-6.62, -66.65) * mm});
            skLineSegment(sketch, "E64", {"start": v(-6.62, -66.65) * mm, "end": v(-6.62, -65.67) * mm});
            skLineSegment(sketch, "E65", {"start": v(-6.62, -65.67) * mm, "end": v(-6.62, 13.13) * mm});
            skLineSegment(sketch, "E66", {"start": v(-6.62, 13.13) * mm, "end": v(0, 13.13) * mm});
            skLineSegment(sketch, "E67", {"start": v(0, 13.13) * mm, "end": v(-5.94, 13.13) * mm});
            skLineSegment(sketch, "E68", {"start": v(-5.94, 13.13) * mm, "end": v(-5.94, 15.12) * mm});
            skLineSegment(sketch, "E69", {"start": v(-5.94, 15.12) * mm, "end": v(0, 15.12) * mm});
            skLineSegment(sketch, "E70", {"start": v(0, 15.12) * mm, "end": v(-7.2, 15.12) * mm});
            skLineSegment(sketch, "E71", {"start": v(-7.2, 15.12) * mm, "end": v(-7.2, 22.6) * mm});
            skLineSegment(sketch, "E72", {"start": v(-7.2, 22.6) * mm, "end": v(0, 22.6) * mm});
            skLineSegment(sketch, "E73", {"start": v(0, 22.6) * mm, "end": v(-3.6, 22.6) * mm});
            skLineSegment(sketch, "E74", {"start": v(-3.6, 22.6) * mm, "end": v(-3.6, 28.33) * mm});
            skLineSegment(sketch, "E75", {"start": v(-3.6, 28.33) * mm, "end": v(0, 28.33) * mm});
            skSolve(sketch);
        }
        {
            var Q0;
            {var subQ0=sQuery(id+"F10.wireOp",EDGE,"E63");Q0=makeQuery(id+"F10.imprint","IMPRINT",FACE,{"disambiguationData":[TD([[makeQuery(id+"F10.imprint","IMPRINT",EDGE,{"derivedFrom":subQ0}),-1.0]])]});}
            var Q1;
            {var subQ0=sQuery(id+"F10.wireOp",EDGE,"E67");Q1=makeQuery(id+"F10.imprint","IMPRINT",FACE,{"disambiguationData":[TD([[makeQuery(id+"F10.imprint","IMPRINT",EDGE,{"derivedFrom":subQ0}),-1.0]])]});}
            var Q2;
            {var subQ0=sQuery(id+"F10.wireOp",EDGE,"E71");Q2=makeQuery(id+"F10.imprint","IMPRINT",FACE,{"disambiguationData":[TD([[makeQuery(id+"F10.imprint","IMPRINT",EDGE,{"derivedFrom":subQ0}),-1.0]])]});}
            var Q3;
            {var subQ2=sQuery(id+"F10.wireOp",EDGE,"E73");Q3=makeQuery(id+"F10.imprint","IMPRINT",FACE,{"disambiguationData":[TD([[makeQuery(id+"F10.imprint","IMPRINT",EDGE,{"derivedFrom":subQ2}),-1.0]])]});}
            var Q4;
            Q4=sQuery(id+"F10.wireOp",EDGE,"E62");
            revolve(context, id + "F11", {"operationType" : NewBodyOperationType.ADD, "entities" : qUnion([Q0, Q1, Q2, Q3]), "axis" : qUnion([Q4]), "revolveType" : RevolveType.FULL});
        }
        {
            var Q0;
            Q0=makeQuery(id+"F11.opRevolve","SWEPT_EDGE",EDGE,{"disambiguationData":[OSD([sQuery(id+"F10.wireOp",EDGE,"E71"),sQuery(id+"F10.wireOp",EDGE,"E72")])]});
            chamfer(context, id + "F12", {"entities" : qUnion([Q0]), "width" : 5.08 * mm, "tangentPropagation" : true});
        }
        {
            var Q0;
            Q0=makeQuery(id+"F11.opRevolve","SWEPT_EDGE",EDGE,{"disambiguationData":[OSD([sQuery(id+"F10.wireOp",EDGE,"E65"),sQuery(id+"F10.wireOp",EDGE,"E66")])]});
            var Q1;
            Q1=makeQuery(id+"F11.opRevolve","SWEPT_EDGE",EDGE,{"disambiguationData":[OSD([sQuery(id+"F10.wireOp",EDGE,"E70"),sQuery(id+"F10.wireOp",EDGE,"E71")])]});
            var Q2;
            Q2=makeQuery(id+"F11.opRevolve","SWEPT_EDGE",EDGE,{"disambiguationData":[OSD([sQuery(id+"F10.wireOp",EDGE,"E63"),sQuery(id+"F10.wireOp",EDGE,"E64")])]});
            chamfer(context, id + "F13", {"entities" : qUnion([Q0, Q1, Q2]), "width" : 0.76 * mm, "tangentPropagation" : true});
        }
        {
            var Q0;
            Q0=qCreatedBy(makeId("Front.planeOp"),FACE);
            var sketch = newSketch(context, id + "F14", { "sketchPlane" : qUnion([Q0])});
            skCircle(sketch, "E76", {"center": v(1.96, -4.11) * mm, "radius": 5 * mm});
            skCircle(sketch, "E77", {"center": v(1.96, -4.11) * mm, "radius": 2.19 * mm});
            skCircle(sketch, "E78", {"center": v(1.96, -55.7) * mm, "radius": 4.07 * mm});
            skCircle(sketch, "E79", {"center": v(1.96, -55.7) * mm, "radius": 1.77 * mm});
            skLineSegment(sketch, "E80", {"start": v(4.86, -8.18) * mm, "end": v(12.6, -9.86) * mm});
            skLineSegment(sketch, "E81", {"start": v(6.03, -1.21) * mm, "end": v(17.32, -7.88) * mm});
            skLineSegment(sketch, "E82", {"start": v(1.14, -51.73) * mm, "end": v(1.24, -51.69) * mm});
            skLineSegment(sketch, "E83", {"start": v(4.22, -59.08) * mm, "end": v(13.95, -52.62) * mm});
            skArc(sketch, "E84", {"start": v(1.14, -51.73) * mm, "mid": v(23.12, -35.24) * mm, "end": v(12.6, -9.86) * mm});
            skArc(sketch, "E85", {"start": v(13.95, -52.62) * mm, "mid": v(26.58, -31.08) * mm, "end": v(17.32, -7.88) * mm});
            skSolve(sketch);
        }
        {
            var Q0;
            Q0=sQuery(id+"F14.wireOp",EDGE,"E77");
            var Q1;
            Q1=sQuery(id+"F14.wireOp",EDGE,"E76");
            var Q2;
            Q2=sQuery(id+"F14.wireOp",EDGE,"E78");
            var Q3;
            Q3=sQuery(id+"F14.wireOp",EDGE,"E79");
            extrude(context, id + "F15", {"bodyType" : ToolBodyType.SURFACE, "surfaceEntities" : qUnion([Q0, Q1, Q2, Q3]), "endBound" : BoundingType.SYMMETRIC, "depth" : 14.86 * mm});
        }
        {
            var Q0;
            {var subQ1=sQuery(id+"F14.wireOp",EDGE,"E80");Q0=makeQuery(id+"F14.imprint","IMPRINT",FACE,{"disambiguationData":[TD([[makeQuery(id+"F14.imprint","IMPRINT",EDGE,{"derivedFrom":subQ1}),1.0]])]});}
            extrude(context, id + "F16", {"entities" : qUnion([Q0]), "operationType" : NewBodyOperationType.ADD, "endBound" : BoundingType.SYMMETRIC, "depth" : 6.35 * mm});
        }
        {
            var Q0;
            Q0=makeQuery(id+"F16.opExtrude","CAP_EDGE",EDGE,{"disambiguationData":[OSD([sQuery(id+"F14.wireOp",EDGE,"E81")])],"isStart":false});
            var Q1;
            Q1=makeQuery(id+"F16.opExtrude","CAP_EDGE",EDGE,{"disambiguationData":[OSD([sQuery(id+"F14.wireOp",EDGE,"E85")])],"isStart":false});
            var Q2;
            Q2=makeQuery(id+"F16.opExtrude","CAP_EDGE",EDGE,{"disambiguationData":[OSD([sQuery(id+"F14.wireOp",EDGE,"E80")])],"isStart":false});
            var Q3;
            Q3=makeQuery(id+"F16.opExtrude","CAP_EDGE",EDGE,{"disambiguationData":[OSD([sQuery(id+"F14.wireOp",EDGE,"E84")])],"isStart":false});
            var Q4;
            Q4=makeQuery(id+"F16.opExtrude","CAP_EDGE",EDGE,{"disambiguationData":[OSD([sQuery(id+"F14.wireOp",EDGE,"E85")])],"isStart":true});
            var Q5;
            Q5=makeQuery(id+"F16.opExtrude","CAP_EDGE",EDGE,{"disambiguationData":[OSD([sQuery(id+"F14.wireOp",EDGE,"E81")])],"isStart":true});
            var Q6;
            Q6=makeQuery(id+"F16.opExtrude","CAP_EDGE",EDGE,{"disambiguationData":[OSD([sQuery(id+"F14.wireOp",EDGE,"E84")])],"isStart":true});
            chamfer(context, id + "F17", {"entities" : qUnion([Q0, Q1, Q2, Q3, Q4, Q5, Q6]), "width" : 0.5 * mm, "tangentPropagation" : true});
        }
    });
